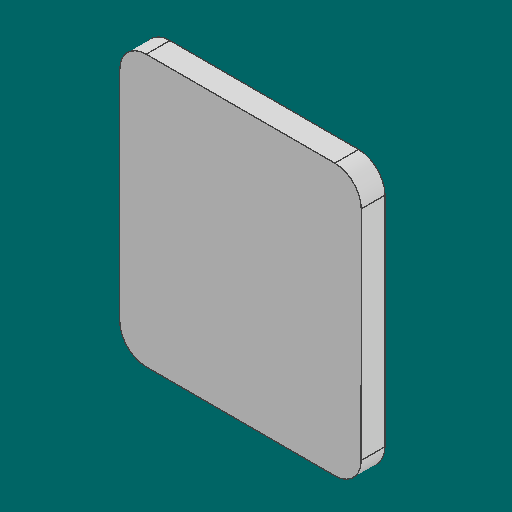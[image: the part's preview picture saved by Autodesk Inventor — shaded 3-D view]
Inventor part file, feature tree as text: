
AUTODESK INVENTOR PART (.ipt)
format: ipt  version: 2025.2 (Build 292293000, 293)  size: 273,408 bytes
history: native  units: mm
features: reference x29, extrude x6, sketch x6, other x4, plane x2, fillet x1
ambient origin geometry x8: Origin, YZ Plane, XZ Plane, XY Plane, X Axis, Y Axis, Z Axis, Center Point
bodies: Solid1 (feature_tree)
feature tree (48):
  plane  "Work Plane1"
  extrude  "Extrusion1"  Depth=2.0mm TaperAngle=0.0deg
  extrude  "Extrusion2"  Depth=7.0mm
  fillet  "Fillet1"  Radius=0.1mm
  sketch  "Sketch3"  dims[d7=0.1mm d8=0.1mm]
  plane  "Work Plane2"
  extrude  "Extrusion3"  Depth=0.1mm
  extrude  "Extrusion4"  Depth=1.0mm
  extrude  "Extrusion5"  Depth=3.0mm
  extrude  "Extrusion6"  Depth=1.0mm TaperAngle=0.0deg
  sketch  "Sketch1"  dims[d0=1.0mm d1=2.0mm d2=0.0mm]
  reference  "Reference1"
  reference  "Reference2"
  reference  "Reference3"
  reference  "Reference4"
  reference  "Reference5"
  reference  "Reference6"
  reference  "Reference7"
  reference  "Reference8"
  reference  "Reference9"
  reference  "Reference10"
  reference  "Reference11"
  reference  "Reference12"
  reference  "Reference13"
  reference  "Reference14"
  reference  "Reference15"
  reference  "Reference16"
  sketch  "Sketch2"  dims[d3=7.0mm d4=0.0mm d5=0.1mm d6=0.1mm]
  reference  "Reference17"
  reference  "Reference18"
  reference  "Reference19"
  reference  "Reference20"
  reference  "Reference21"
  sketch  "Sketch4"  dims[d9=1.0mm d10=1.5mm]
  sketch  "Sketch5"  dims[d11=3.88mm d12=0.0mm d13=3.0mm]
  sketch  "Sketch6"  dims[d14=10.0mm d15=0.0mm d16=1.0mm d17=0.0mm d18=20.0mm d19=20.0mm d20=5.65mm d21=0.0mm d22=0.5mm]
  reference  "Reference22"
  reference  "Reference23"
  reference  "Reference24"
  reference  "Reference25"
  reference  "Reference26"
  reference  "Reference27"
  reference  "Reference28"
  reference  "Reference29"
  other  "<userpath>\Downloads\cassing_hardware\Assembly1.iam"
  other  "Assembly1.iam"
  other  "AVR_MasImam:1"
  other  "ARDUINO-UNO_20:1"
